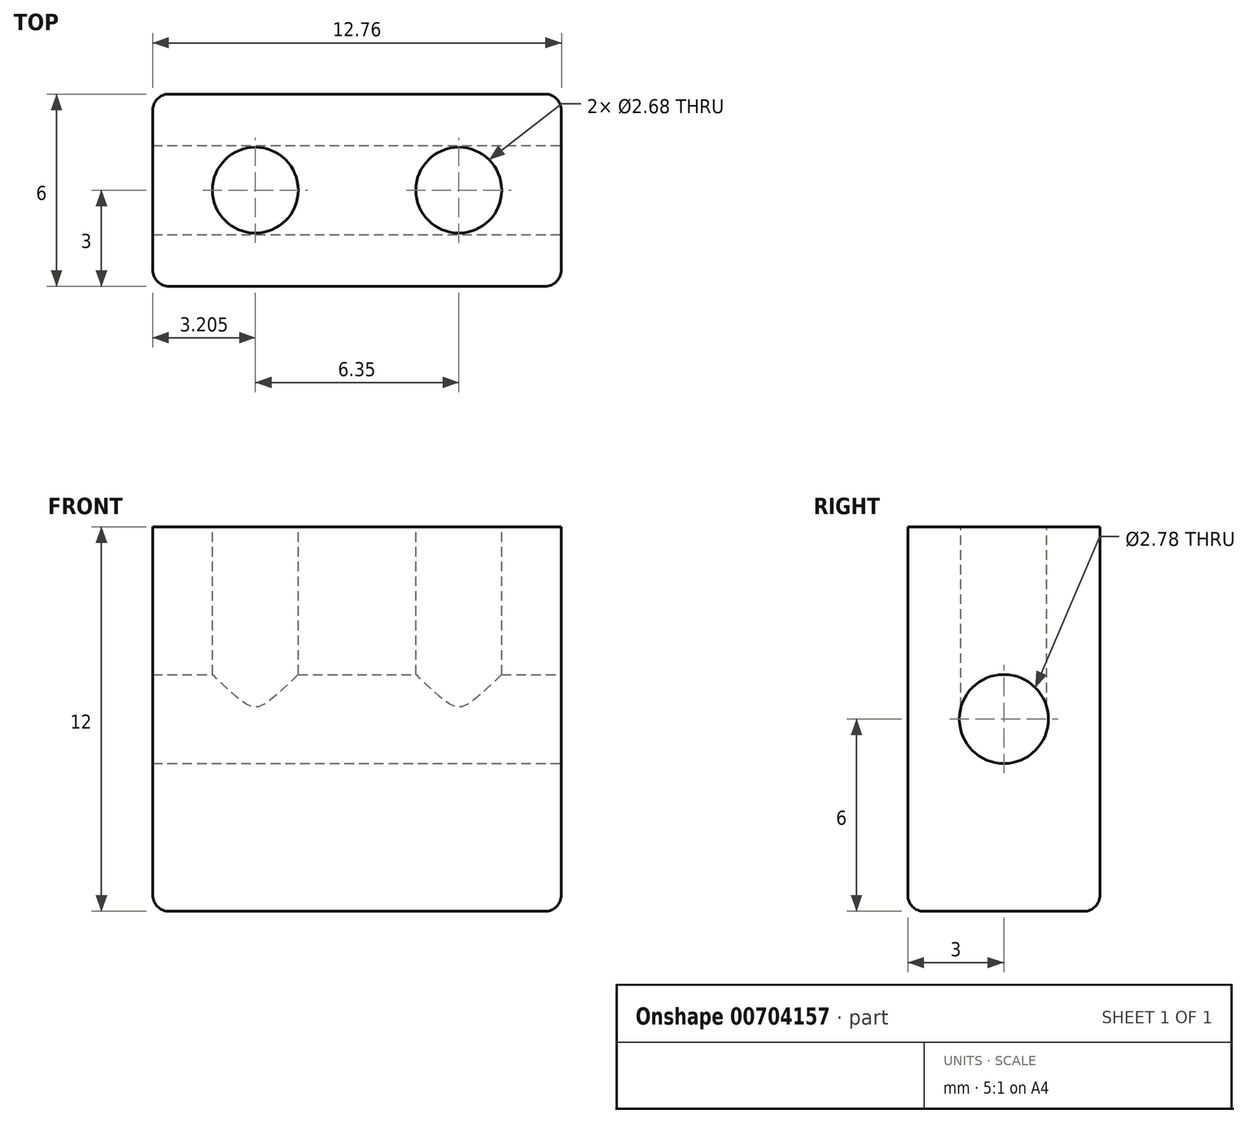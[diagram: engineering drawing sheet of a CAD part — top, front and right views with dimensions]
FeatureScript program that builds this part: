
annotation { "Feature Type Name" : "Feature", "Feature Type Description" : "" }
export const myFeature = defineFeature(function(context is Context, id is Id, definition is map)
    precondition{}
    {
        {
            var Q0;
            Q0=qCreatedBy(makeId("Top.planeOp"),FACE);
            var sketch = newSketch(context, id + "F0", { "sketchPlane" : qUnion([Q0])});
            skLineSegment(sketch, "E0.bottom", {"start": v(6.38, 3) * mm, "end": v(-6.38, 3) * mm});
            skLineSegment(sketch, "E0.top", {"start": v(6.38, -3) * mm, "end": v(-6.38, -3) * mm});
            skLineSegment(sketch, "E0.left", {"start": v(6.38, 3) * mm, "end": v(6.38, -3) * mm});
            skLineSegment(sketch, "E0.right", {"start": v(-6.38, 3) * mm, "end": v(-6.38, -3) * mm});
            skPoint(sketch, "E0.middle", {"position": v(0, 0) * mm});
            skSolve(sketch);
        }
        {
            var Q0;
            Q0 = qSketchRegion(id + "F0", true);
            extrude(context, id + "F1", {"entities" : qUnion([Q0]), "endBound" : BoundingType.SYMMETRIC, "depth" : 12 * mm, "offsetDistance" : 25 * mm});
        }
        {
            var Q0;
            Q0=makeQuery(id+"F1.opExtrude","SWEPT_FACE",FACE,{"disambiguationData":[OSD([sQuery(id+"F0.wireOp",EDGE,"E0.left")])]});
            var sketch = newSketch(context, id + "F2", { "sketchPlane" : qUnion([Q0])});
            skCircle(sketch, "E1", {"center": v(0, 0) * mm, "radius": 1.39 * mm});
            skSolve(sketch);
        }
        {
            var Q0;
            Q0 = qSketchRegion(id + "F2", true);
            extrude(context, id + "F3", {"entities" : qUnion([Q0]), "operationType" : NewBodyOperationType.REMOVE, "endBound" : BoundingType.THROUGH_ALL, "oppositeDirection" : true, "depth" : 25 * mm, "offsetDistance" : 25 * mm});
        }
        {
            var Q0;
            Q0=makeQuery(id+"F1.opExtrude","CAP_FACE",FACE,{"disambiguationData":[OSD([sQuery(id+"F0.wireOp",EDGE,"E0.bottom"),sQuery(id+"F0.wireOp",EDGE,"E0.top"),sQuery(id+"F0.wireOp",EDGE,"E0.left"),sQuery(id+"F0.wireOp",EDGE,"E0.right")])],"isStart":false});
            var sketch = newSketch(context, id + "F4", { "sketchPlane" : qUnion([Q0])});
            skCircle(sketch, "E2", {"center": v(-3.18, 0) * mm, "radius": 1.34 * mm});
            skCircle(sketch, "E3.MirrorC", {"center": v(3.18, 0) * mm, "radius": 1.34 * mm});
            skSolve(sketch);
        }
        {
            var Q0;
            Q0 = qSketchRegion(id + "F4", true);
            extrude(context, id + "F5", {"entities" : qUnion([Q0]), "operationType" : NewBodyOperationType.REMOVE, "oppositeDirection" : true, "depth" : 6.35 * mm, "offsetDistance" : 25 * mm});
        }
        {
            var Q0;
            Q0=makeQuery(id+"F1.opExtrude","CAP_EDGE",EDGE,{"disambiguationData":[OSD([sQuery(id+"F0.wireOp",EDGE,"E0.bottom")])],"isStart":true});
            var Q1;
            Q1=makeQuery(id+"F1.opExtrude","SWEPT_EDGE",EDGE,{"disambiguationData":[OSD([sQuery(id+"F0.wireOp",EDGE,"E0.bottom"),sQuery(id+"F0.wireOp",EDGE,"E0.left")])]});
            var Q2;
            Q2=makeQuery(id+"F1.opExtrude","CAP_EDGE",EDGE,{"disambiguationData":[OSD([sQuery(id+"F0.wireOp",EDGE,"E0.left")])],"isStart":true});
            var Q3;
            Q3=makeQuery(id+"F1.opExtrude","SWEPT_EDGE",EDGE,{"disambiguationData":[OSD([sQuery(id+"F0.wireOp",EDGE,"E0.top"),sQuery(id+"F0.wireOp",EDGE,"E0.left")])]});
            var Q4;
            Q4=makeQuery(id+"F1.opExtrude","CAP_EDGE",EDGE,{"disambiguationData":[OSD([sQuery(id+"F0.wireOp",EDGE,"E0.top")])],"isStart":true});
            var Q5;
            Q5=makeQuery(id+"F1.opExtrude","CAP_EDGE",EDGE,{"disambiguationData":[OSD([sQuery(id+"F0.wireOp",EDGE,"E0.right")])],"isStart":true});
            var Q6;
            Q6=makeQuery(id+"F1.opExtrude","SWEPT_EDGE",EDGE,{"disambiguationData":[OSD([sQuery(id+"F0.wireOp",EDGE,"E0.bottom"),sQuery(id+"F0.wireOp",EDGE,"E0.right")])]});
            var Q7;
            Q7=makeQuery(id+"F1.opExtrude","SWEPT_EDGE",EDGE,{"disambiguationData":[OSD([sQuery(id+"F0.wireOp",EDGE,"E0.top"),sQuery(id+"F0.wireOp",EDGE,"E0.right")])]});
            fillet(context, id + "F6", {"entities" : qUnion([Q0, Q1, Q2, Q3, Q4, Q5, Q6, Q7]), "radius" : 0.5 * mm, "tangentPropagation" : true, "allowEdgeOverflow" : false});
        }
    });
